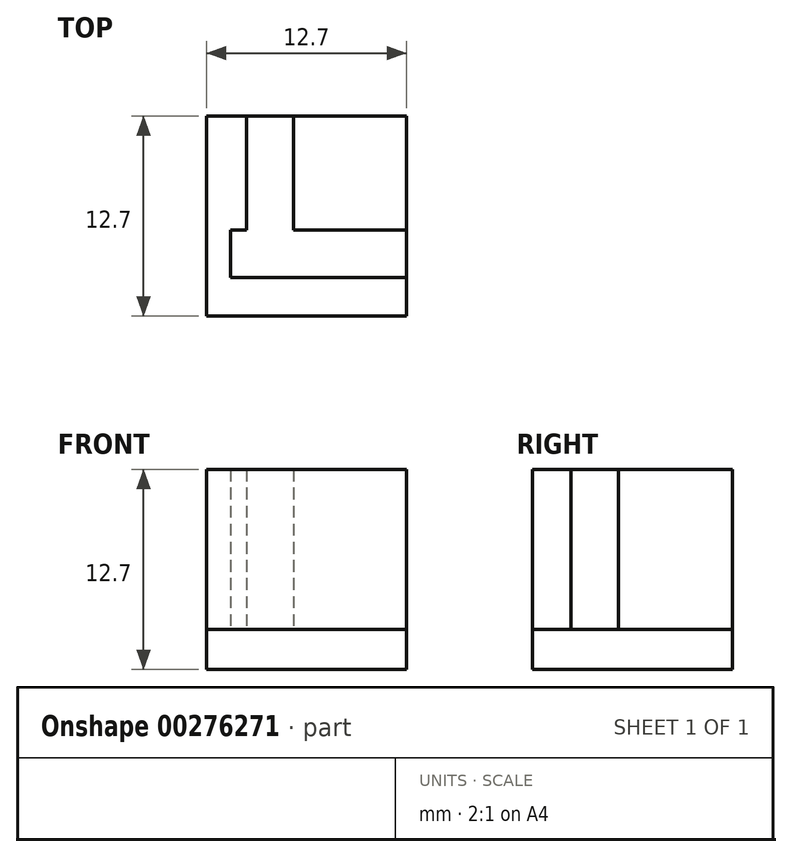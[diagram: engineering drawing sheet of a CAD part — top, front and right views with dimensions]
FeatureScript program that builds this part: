
annotation { "Feature Type Name" : "Feature", "Feature Type Description" : "" }
export const myFeature = defineFeature(function(context is Context, id is Id, definition is map)
    precondition{}
    {
        {
            var Q0;
            Q0=qCreatedBy(makeId("Top.planeOp"),FACE);
            var sketch = newSketch(context, id + "F0", { "sketchPlane" : qUnion([Q0])});
            skLineSegment(sketch, "E0.bottom", {"start": v(-14.96, 0.92) * mm, "end": v(-2.26, 0.92) * mm});
            skLineSegment(sketch, "E0.top", {"start": v(-14.96, -11.78) * mm, "end": v(-2.26, -11.78) * mm});
            skLineSegment(sketch, "E0.left", {"start": v(-14.96, 0.92) * mm, "end": v(-14.96, -11.78) * mm});
            skLineSegment(sketch, "E0.right", {"start": v(-2.26, 0.92) * mm, "end": v(-2.26, -11.78) * mm});
            skLineSegment(sketch, "E1.bottom", {"start": v(-12.42, 0.92) * mm, "end": v(-9.42, 0.92) * mm});
            skLineSegment(sketch, "E1.top", {"start": v(-12.42, -9.32) * mm, "end": v(-9.42, -9.32) * mm});
            skLineSegment(sketch, "E1.left", {"start": v(-12.42, 0.92) * mm, "end": v(-12.42, -6.32) * mm});
            skLineSegment(sketch, "E1.right", {"start": v(-9.42, 0.92) * mm, "end": v(-9.42, -6.32) * mm});
            skLineSegment(sketch, "E2.bottom", {"start": v(-13.44, -6.32) * mm, "end": v(-12.42, -6.32) * mm});
            skLineSegment(sketch, "E2.top", {"start": v(-13.44, -9.32) * mm, "end": v(-2.26, -9.32) * mm});
            skLineSegment(sketch, "E2.left", {"start": v(-13.44, -6.32) * mm, "end": v(-13.44, -9.32) * mm});
            skLineSegment(sketch, "E2.right", {"start": v(-2.26, -6.32) * mm, "end": v(-2.26, -9.32) * mm});
            skLineSegment(sketch, "E3.trimOffspring", {"start": v(-9.42, -6.32) * mm, "end": v(-2.26, -6.32) * mm});
            skSolve(sketch);
        }
        {
            var Q0;
            {var subQ3=sQuery(id+"F0.wireOp",EDGE,"E1.right");Q0=makeQuery(id+"F0.imprint","IMPRINT",FACE,{"disambiguationData":[TD([[makeQuery(id+"F0.imprint","IMPRINT",EDGE,{"derivedFrom":subQ3}),1.0]])]});}
            var Q1;
            {var subQ1=sQuery(id+"F0.wireOp",EDGE,"E0.top");Q1=makeQuery(id+"F0.imprint","IMPRINT",FACE,{"disambiguationData":[TD([[makeQuery(id+"F0.imprint","IMPRINT",EDGE,{"derivedFrom":subQ1}),1.0]])]});}
            extrude(context, id + "F1", {"entities" : qUnion([Q0, Q1]), "depth" : 10.16 * mm});
        }
        {
            var Q0;
            Q0=makeQuery(id+"F1.opExtrude","CAP_FACE",FACE,{"disambiguationData":[OSD([sQuery(id+"F0.wireOp",EDGE,"E0.bottom"),sQuery(id+"F0.wireOp",EDGE,"E0.right"),sQuery(id+"F0.wireOp",EDGE,"E1.right"),sQuery(id+"F0.wireOp",EDGE,"E3.trimOffspring")])],"isStart":true});
            var sketch = newSketch(context, id + "F2", { "sketchPlane" : qUnion([Q0])});
            skLineSegment(sketch, "E4.0.0", {"start": v(-13.44, 9.32) * mm, "end": v(-2.26, 9.32) * mm});
            skLineSegment(sketch, "E4.0.1", {"start": v(-2.26, 9.32) * mm, "end": v(-2.26, 11.78) * mm});
            skLineSegment(sketch, "E4.0.2", {"start": v(-2.26, 11.78) * mm, "end": v(-14.96, 11.78) * mm});
            skLineSegment(sketch, "E4.0.3", {"start": v(-14.96, 11.78) * mm, "end": v(-14.96, -0.92) * mm});
            skLineSegment(sketch, "E4.0.4", {"start": v(-14.96, -0.92) * mm, "end": v(-12.42, -0.92) * mm});
            skLineSegment(sketch, "E4.0.5", {"start": v(-12.42, -0.92) * mm, "end": v(-12.42, 6.32) * mm});
            skLineSegment(sketch, "E4.0.6", {"start": v(-12.42, 6.32) * mm, "end": v(-13.44, 6.32) * mm});
            skLineSegment(sketch, "E4.0.7", {"start": v(-13.44, 6.32) * mm, "end": v(-13.44, 9.32) * mm});
            skLineSegment(sketch, "E5.0.0", {"start": v(-9.42, 6.32) * mm, "end": v(-9.42, -0.92) * mm});
            skLineSegment(sketch, "E5.0.1", {"start": v(-9.42, -0.92) * mm, "end": v(-2.26, -0.92) * mm});
            skLineSegment(sketch, "E5.0.2", {"start": v(-2.26, -0.92) * mm, "end": v(-2.26, 6.32) * mm});
            skLineSegment(sketch, "E5.0.3", {"start": v(-2.26, 6.32) * mm, "end": v(-9.42, 6.32) * mm});
            skLineSegment(sketch, "E6.bottom", {"start": v(-2.26, -0.92) * mm, "end": v(-14.96, -0.92) * mm});
            skLineSegment(sketch, "E6.left", {"start": v(-2.26, -0.92) * mm, "end": v(-2.26, 11.78) * mm});
            skLineSegment(sketch, "E6.right", {"start": v(-14.96, -0.92) * mm, "end": v(-14.96, 11.78) * mm});
            skSolve(sketch);
        }
        {
            var Q0;
            {var subQ0=sQuery(id+"F2.wireOp",EDGE,"E5.0.0");Q0=makeQuery(id+"F2.imprint","IMPRINT",FACE,{"disambiguationData":[TD([[makeQuery(id+"F2.imprint","IMPRINT",EDGE,{"derivedFrom":subQ0}),-1.0]])]});}
            var Q1;
            {var subQ1=sQuery(id+"F2.wireOp",EDGE,"E4.0.0");Q1=makeQuery(id+"F2.imprint","IMPRINT",FACE,{"disambiguationData":[TD([[makeQuery(id+"F2.imprint","IMPRINT",EDGE,{"derivedFrom":subQ1}),-1.0]])]});}
            var Q2;
            {var subQ2=sQuery(id+"F2.wireOp",EDGE,"E4.0.0");Q2=makeQuery(id+"F2.imprint","IMPRINT",FACE,{"disambiguationData":[TD([[makeQuery(id+"F2.imprint","IMPRINT",EDGE,{"derivedFrom":subQ2}),1.0]])]});}
            extrude(context, id + "F3", {"entities" : qUnion([Q0, Q1, Q2]), "depth" : 2.54 * mm});
        }
    });
